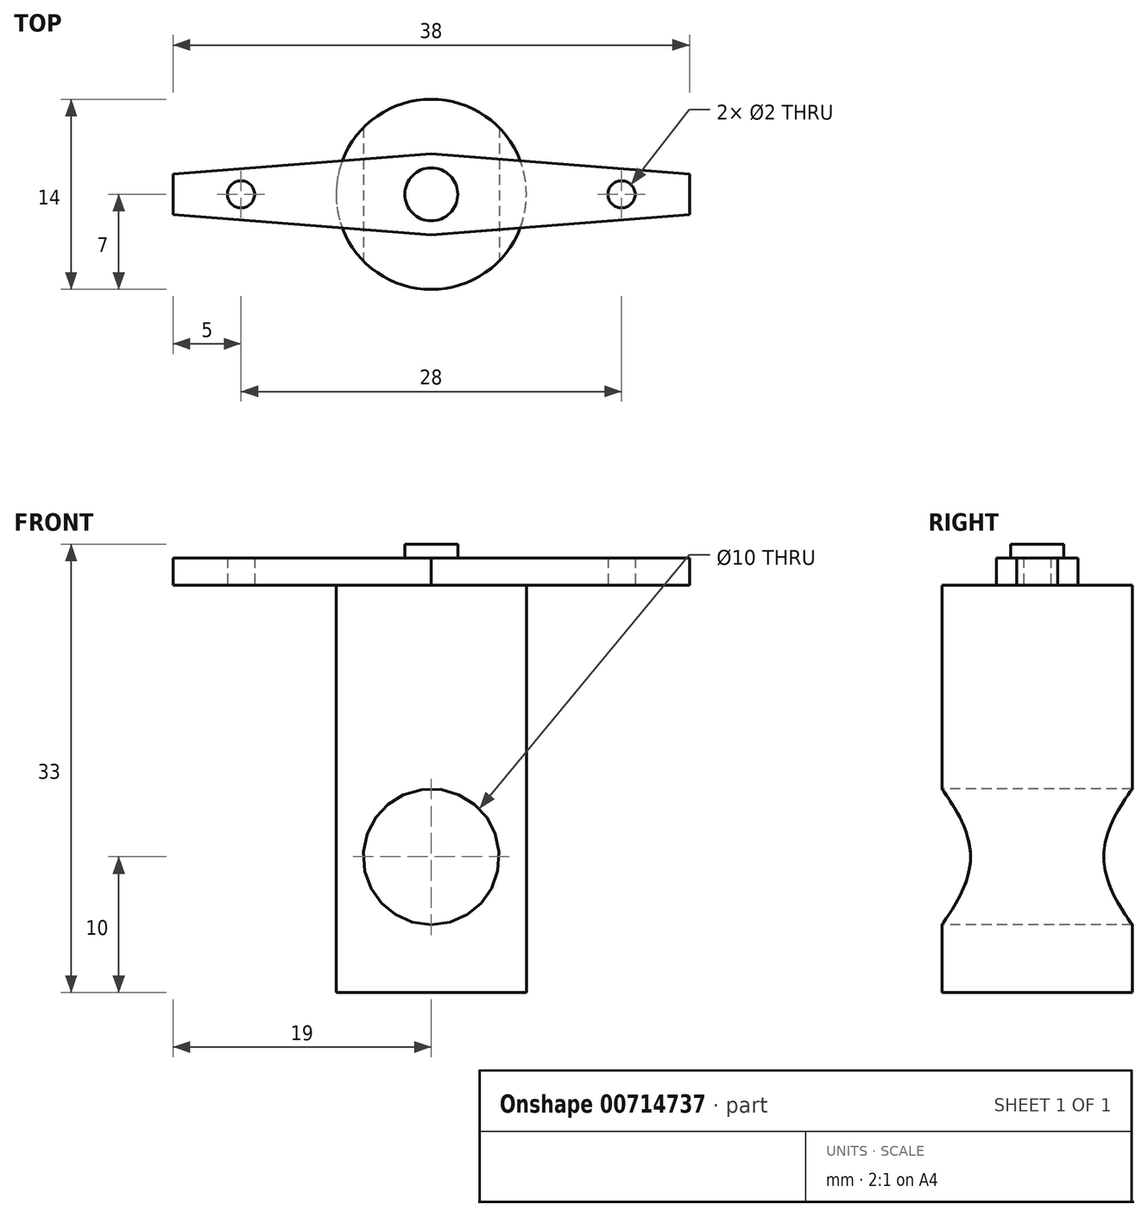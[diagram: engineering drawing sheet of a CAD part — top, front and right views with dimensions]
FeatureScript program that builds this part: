
annotation { "Feature Type Name" : "Feature", "Feature Type Description" : "" }
export const myFeature = defineFeature(function(context is Context, id is Id, definition is map)
    precondition{}
    {
        {
            var Q0;
            Q0=qCreatedBy(makeId("Top.planeOp"),FACE);
            var sketch = newSketch(context, id + "F0", { "sketchPlane" : qUnion([Q0])});
            skLineSegment(sketch, "E0", {"start": v(0, 0) * mm, "end": v(-14, 0) * mm, "construction": true});
            skLineSegment(sketch, "E1", {"start": v(14, 0) * mm, "end": v(0, 0) * mm, "construction": true});
            skCircle(sketch, "E2", {"center": v(-14, 0) * mm, "radius": 1 * mm});
            skCircle(sketch, "E3", {"center": v(14, 0) * mm, "radius": 1 * mm});
            skLineSegment(sketch, "E4", {"start": v(0, 0) * mm, "end": v(-19, 0) * mm, "construction": true});
            skLineSegment(sketch, "E5", {"start": v(0, 0) * mm, "end": v(19, 0) * mm, "construction": true});
            skLineSegment(sketch, "E6", {"start": v(0, 0) * mm, "end": v(0, 3) * mm});
            skLineSegment(sketch, "E7", {"start": v(0, 0) * mm, "end": v(0, -3) * mm});
            skLineSegment(sketch, "E8", {"start": v(-19, 0) * mm, "end": v(-19, 1.5) * mm});
            skLineSegment(sketch, "E9", {"start": v(-19, 0) * mm, "end": v(-19, -1.5) * mm});
            skLineSegment(sketch, "E10", {"start": v(-19, 1.5) * mm, "end": v(0, 3) * mm});
            skLineSegment(sketch, "E11", {"start": v(0, -3) * mm, "end": v(-19, -1.5) * mm});
            skLineSegment(sketch, "E12", {"start": v(19, 0) * mm, "end": v(19, -1.5) * mm});
            skLineSegment(sketch, "E13", {"start": v(19, 0) * mm, "end": v(19, 1.5) * mm});
            skLineSegment(sketch, "E14", {"start": v(19, -1.5) * mm, "end": v(0, -3) * mm});
            skLineSegment(sketch, "E15", {"start": v(0, 3) * mm, "end": v(19, 1.5) * mm});
            skSolve(sketch);
        }
        {
            var Q0;
            Q0=makeQuery(id+"F0.imprint","IMPRINT",FACE,{"disambiguationData":[TD([[makeQuery(id+"F0.imprint","IMPRINT",EDGE,{"derivedFrom":sQuery(id+"F0.wireOp",EDGE,"E2")}),-1.0]])]});
            var Q1;
            Q1=makeQuery(id+"F0.imprint","IMPRINT",FACE,{"disambiguationData":[TD([[makeQuery(id+"F0.imprint","IMPRINT",EDGE,{"derivedFrom":sQuery(id+"F0.wireOp",EDGE,"E3")}),-1.0]])]});
            extrude(context, id + "F1", {"entities" : qUnion([Q0, Q1]), "depth" : 2 * mm, "offsetDistance" : 25 * mm});
        }
        {
            var Q0;
            Q0=makeQuery(id+"F1.opExtrude","CAP_FACE",FACE,{"disambiguationData":[OSD([sQuery(id+"F0.wireOp",EDGE,"E2"),sQuery(id+"F0.wireOp",EDGE,"E3"),sQuery(id+"F0.wireOp",EDGE,"E8"),sQuery(id+"F0.wireOp",EDGE,"E9"),sQuery(id+"F0.wireOp",EDGE,"E10"),sQuery(id+"F0.wireOp",EDGE,"E11"),sQuery(id+"F0.wireOp",EDGE,"E12"),sQuery(id+"F0.wireOp",EDGE,"E13"),sQuery(id+"F0.wireOp",EDGE,"E14"),sQuery(id+"F0.wireOp",EDGE,"E15")])],"isStart":false});
            var sketch = newSketch(context, id + "F2", { "sketchPlane" : qUnion([Q0])});
            skCircle(sketch, "E16", {"center": v(0, 0) * mm, "radius": 1.95 * mm});
            skSolve(sketch);
        }
        {
            var Q0;
            Q0=makeQuery(id+"F2.imprint","IMPRINT",FACE,{"disambiguationData":[TD([[makeQuery(id+"F2.imprint","IMPRINT",EDGE,{"derivedFrom":sQuery(id+"F2.wireOp",EDGE,"E16")}),1.0]])]});
            extrude(context, id + "F3", {"entities" : qUnion([Q0]), "operationType" : NewBodyOperationType.ADD, "depth" : 1 * mm, "offsetDistance" : 25 * mm});
        }
        {
            var Q0;
            Q0=makeQuery(id+"F1.opExtrude","CAP_FACE",FACE,{"disambiguationData":[OSD([sQuery(id+"F0.wireOp",EDGE,"E2"),sQuery(id+"F0.wireOp",EDGE,"E3"),sQuery(id+"F0.wireOp",EDGE,"E8"),sQuery(id+"F0.wireOp",EDGE,"E9"),sQuery(id+"F0.wireOp",EDGE,"E10"),sQuery(id+"F0.wireOp",EDGE,"E11"),sQuery(id+"F0.wireOp",EDGE,"E12"),sQuery(id+"F0.wireOp",EDGE,"E13"),sQuery(id+"F0.wireOp",EDGE,"E14"),sQuery(id+"F0.wireOp",EDGE,"E15")])],"isStart":true});
            var sketch = newSketch(context, id + "F4", { "sketchPlane" : qUnion([Q0])});
            skCircle(sketch, "E17", {"center": v(0, 0) * mm, "radius": 7 * mm});
            skSolve(sketch);
        }
        {
            var Q0;
            {var subQ0=sQuery(id+"F4.wireOp",EDGE,"E17");var subQ1=makeQuery(id+"F1.opExtrude","CAP_EDGE",EDGE,{"disambiguationData":[OSD([sQuery(id+"F0.wireOp",EDGE,"E11")])],"isStart":true});var subQ2=makeQuery(id+"F4.imprint","INTERSECT",VERTEX,{"derivedFrom":[subQ1,subQ0]});Q0=makeQuery(id+"F4.imprint","IMPRINT",FACE,{"disambiguationData":[TD([[makeQuery(id+"F4.imprint","IMPRINT",EDGE,{"disambiguationData":[TD([[subQ2,1.0]])],"derivedFrom":subQ0}),1.0]])]});}
            var Q1;
            {var subQ3=sQuery(id+"F4.wireOp",EDGE,"E17");var subQ8=makeQuery(id+"F1.opExtrude","CAP_EDGE",EDGE,{"disambiguationData":[OSD([sQuery(id+"F0.wireOp",EDGE,"E11")])],"isStart":true});var subQ10=makeQuery(id+"F4.imprint","INTERSECT",VERTEX,{"derivedFrom":[subQ8,subQ3]});Q1=makeQuery(id+"F4.imprint","IMPRINT",FACE,{"disambiguationData":[TD([[makeQuery(id+"F4.imprint","IMPRINT",EDGE,{"disambiguationData":[TD([[subQ10,-1.0]])],"derivedFrom":subQ3}),1.0]])]});}
            var Q2;
            {var subQ0=sQuery(id+"F4.wireOp",EDGE,"E17");var subQ1=makeQuery(id+"F1.opExtrude","CAP_EDGE",EDGE,{"disambiguationData":[OSD([sQuery(id+"F0.wireOp",EDGE,"E10")])],"isStart":true});var subQ2=makeQuery(id+"F4.imprint","INTERSECT",VERTEX,{"derivedFrom":[subQ1,subQ0]});Q2=makeQuery(id+"F4.imprint","IMPRINT",FACE,{"disambiguationData":[TD([[makeQuery(id+"F4.imprint","IMPRINT",EDGE,{"disambiguationData":[TD([[subQ2,-1.0]])],"derivedFrom":subQ0}),1.0]])]});}
            extrude(context, id + "F5", {"entities" : qUnion([Q0, Q1, Q2]), "operationType" : NewBodyOperationType.ADD, "depth" : 30 * mm, "offsetDistance" : 25 * mm});
        }
        {
            var Q0;
            Q0=qCreatedBy(makeId("Front.planeOp"),FACE);
            var sketch = newSketch(context, id + "F6", { "sketchPlane" : qUnion([Q0])});
            skLineSegment(sketch, "E18", {"start": v(0, 0) * mm, "end": v(0, -20) * mm, "construction": true});
            skCircle(sketch, "E19", {"center": v(0, -20) * mm, "radius": 5 * mm});
            skSolve(sketch);
        }
        {
            var Q0;
            Q0 = qSketchRegion(id + "F6", true);
            extrude(context, id + "F7", {"entities" : qUnion([Q0]), "operationType" : NewBodyOperationType.REMOVE, "endBound" : BoundingType.SYMMETRIC, "oppositeDirection" : true, "depth" : 25 * mm, "offsetDistance" : 25 * mm});
        }
    });
